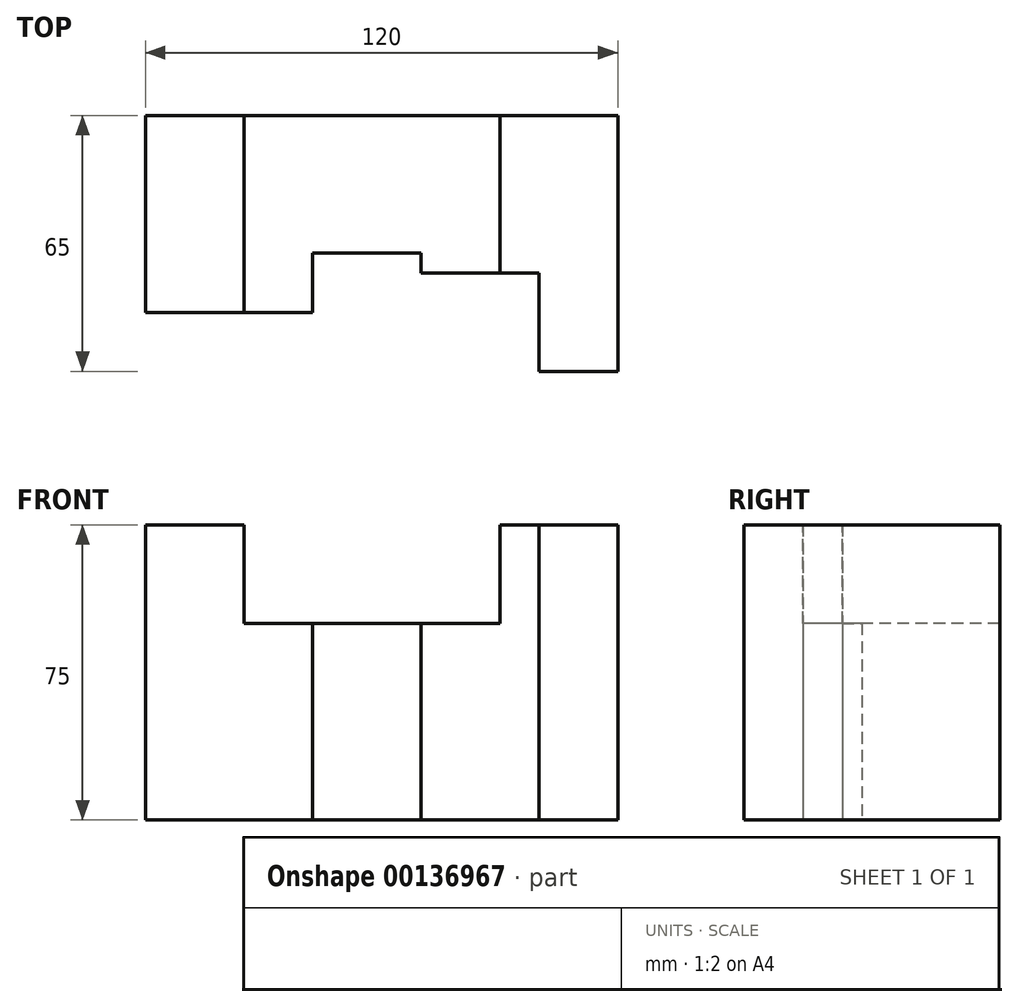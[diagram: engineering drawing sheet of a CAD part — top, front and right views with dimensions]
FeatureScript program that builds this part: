
annotation { "Feature Type Name" : "Feature", "Feature Type Description" : "" }
export const myFeature = defineFeature(function(context is Context, id is Id, definition is map)
    precondition{}
    {
        {
            var Q0;
            Q0=qCreatedBy(makeId("Top.planeOp"),FACE);
            var sketch = newSketch(context, id + "F0", { "sketchPlane" : qUnion([Q0])});
            skLineSegment(sketch, "E0", {"start": v(0, 50) * mm, "end": v(0, 0) * mm});
            skLineSegment(sketch, "E1", {"start": v(0, 50) * mm, "end": v(120, 50) * mm});
            skLineSegment(sketch, "E2", {"start": v(120, 50) * mm, "end": v(120, -15) * mm});
            skLineSegment(sketch, "E3", {"start": v(120, -15) * mm, "end": v(100, -15) * mm});
            skLineSegment(sketch, "E4", {"start": v(70, 10) * mm, "end": v(70, 15) * mm});
            skLineSegment(sketch, "E5", {"start": v(70, 15) * mm, "end": v(42.5, 15) * mm});
            skLineSegment(sketch, "E6", {"start": v(42.5, 15) * mm, "end": v(42.5, 0) * mm});
            skLineSegment(sketch, "E7", {"start": v(42.5, 0) * mm, "end": v(0, 0) * mm});
            skLineSegment(sketch, "E8", {"start": v(100, -15) * mm, "end": v(100, 10) * mm});
            skLineSegment(sketch, "E9", {"start": v(100, 10) * mm, "end": v(70, 10) * mm});
            skSolve(sketch);
        }
        {
            var Q0;
            Q0=makeQuery(id+"F0.imprint","IMPRINT",FACE,{"disambiguationData":[TD([[makeQuery(id+"F0.imprint","IMPRINT",EDGE,{"derivedFrom":sQuery(id+"F0.wireOp",EDGE,"E0")}),1.0]])]});
            extrude(context, id + "F1", {"entities" : qUnion([Q0]), "depth" : 75 * mm});
        }
        {
            var Q0;
            Q0=makeQuery(id+"F1.opExtrude","CAP_FACE",FACE,{"disambiguationData":[OSD([sQuery(id+"F0.wireOp",EDGE,"E0"),sQuery(id+"F0.wireOp",EDGE,"E1"),sQuery(id+"F0.wireOp",EDGE,"E2"),sQuery(id+"F0.wireOp",EDGE,"E3"),sQuery(id+"F0.wireOp",EDGE,"E4"),sQuery(id+"F0.wireOp",EDGE,"E5"),sQuery(id+"F0.wireOp",EDGE,"E6"),sQuery(id+"F0.wireOp",EDGE,"E7"),sQuery(id+"F0.wireOp",EDGE,"E8"),sQuery(id+"F0.wireOp",EDGE,"E9")])],"isStart":false});
            var sketch = newSketch(context, id + "F2", { "sketchPlane" : qUnion([Q0])});
            skLineSegment(sketch, "E10", {"start": v(90, 50) * mm, "end": v(90, 10) * mm});
            skLineSegment(sketch, "E11", {"start": v(100, 10) * mm, "end": v(70, 10) * mm});
            skLineSegment(sketch, "E12", {"start": v(70, 10) * mm, "end": v(70, 15) * mm});
            skLineSegment(sketch, "E13", {"start": v(90, 50) * mm, "end": v(25, 50) * mm});
            skLineSegment(sketch, "E14", {"start": v(25, 50) * mm, "end": v(25, 0) * mm});
            skPoint(sketch, "E14.endSnap0", {"position": v(21.25, 0) * mm});
            skLineSegment(sketch, "E15", {"start": v(25, 0) * mm, "end": v(42.5, 0) * mm});
            skLineSegment(sketch, "E16", {"start": v(42.5, 0) * mm, "end": v(42.5, 15) * mm});
            skLineSegment(sketch, "E17", {"start": v(42.5, 15) * mm, "end": v(70, 15) * mm});
            skSolve(sketch);
        }
        {
            var Q0;
            Q0 = qSketchRegion(id + "F2", true);
            extrude(context, id + "F3", {"entities" : qUnion([Q0]), "operationType" : NewBodyOperationType.REMOVE, "oppositeDirection" : true, "depth" : 25 * mm});
        }
    });
